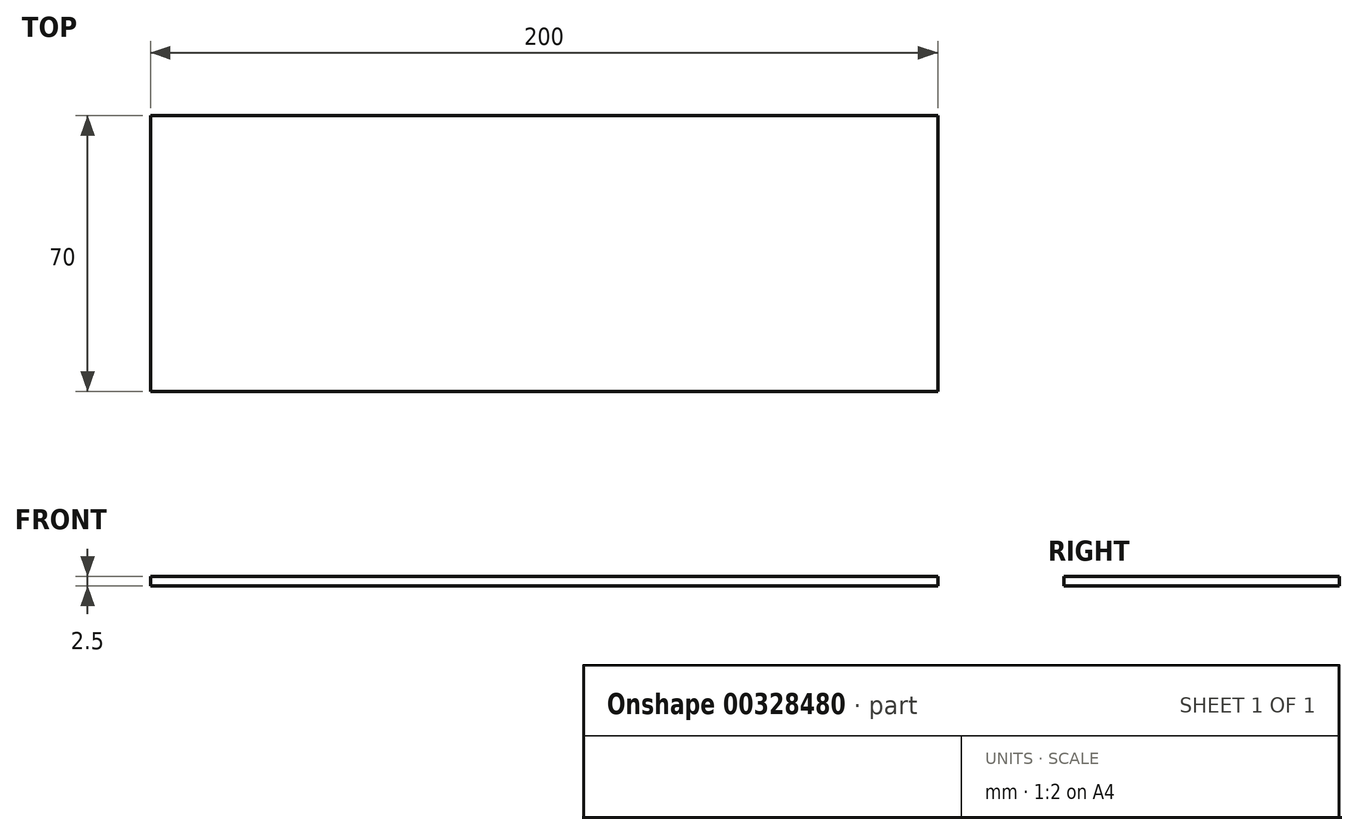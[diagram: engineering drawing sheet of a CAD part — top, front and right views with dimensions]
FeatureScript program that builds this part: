
annotation { "Feature Type Name" : "Feature", "Feature Type Description" : "" }
export const myFeature = defineFeature(function(context is Context, id is Id, definition is map)
    precondition{}
    {
        {
            var Q0;
            Q0=qCreatedBy(makeId("Top.planeOp"),FACE);
            var sketch = newSketch(context, id + "F0", { "sketchPlane" : qUnion([Q0])});
            skLineSegment(sketch, "E0.bottom", {"start": v(100, -35) * mm, "end": v(-100, -35) * mm});
            skLineSegment(sketch, "E0.top", {"start": v(100, 35) * mm, "end": v(-100, 35) * mm});
            skLineSegment(sketch, "E0.left", {"start": v(100, -35) * mm, "end": v(100, 35) * mm});
            skLineSegment(sketch, "E0.right", {"start": v(-100, -35) * mm, "end": v(-100, 35) * mm});
            skPoint(sketch, "E0.middle", {"position": v(0, 0) * mm});
            skSolve(sketch);
        }
        {
            var Q0;
            Q0=makeQuery(id+"F0.imprint","IMPRINT",FACE,{"disambiguationData":[TD([[makeQuery(id+"F0.imprint","IMPRINT",EDGE,{"derivedFrom":sQuery(id+"F0.wireOp",EDGE,"E0.bottom")}),-1.0]])]});
            extrude(context, id + "F1", {"entities" : qUnion([Q0]), "depth" : 2.5 * mm});
        }
    });
